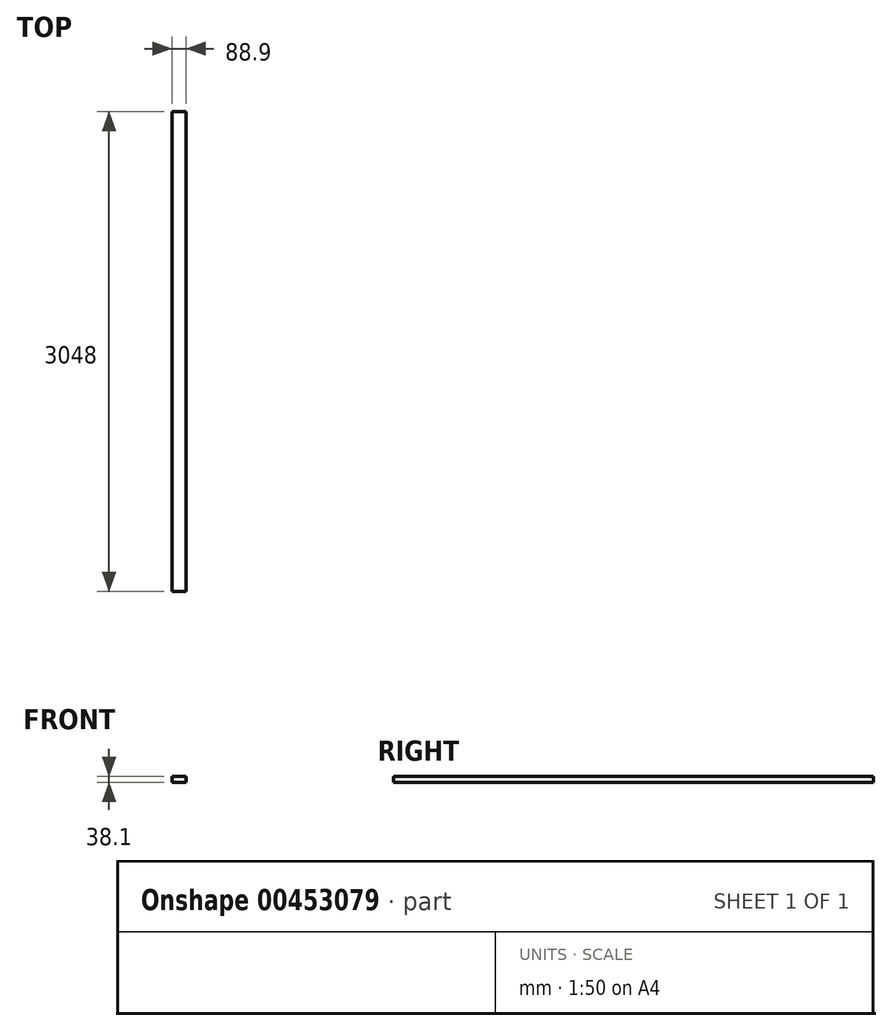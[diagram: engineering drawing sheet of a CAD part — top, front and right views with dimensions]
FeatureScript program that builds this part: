
annotation { "Feature Type Name" : "Feature", "Feature Type Description" : "" }
export const myFeature = defineFeature(function(context is Context, id is Id, definition is map)
    precondition{}
    {
        {
            var Q0;
            Q0=qCreatedBy(makeId("Front.planeOp"),FACE);
            var sketch = newSketch(context, id + "F0", { "sketchPlane" : qUnion([Q0])});
            skLineSegment(sketch, "E0.bottom", {"start": v(44.45, 19.05) * mm, "end": v(-44.45, 19.05) * mm});
            skLineSegment(sketch, "E0.top", {"start": v(44.45, -19.05) * mm, "end": v(-44.45, -19.05) * mm});
            skLineSegment(sketch, "E0.left", {"start": v(44.45, 19.05) * mm, "end": v(44.45, -19.05) * mm});
            skLineSegment(sketch, "E0.right", {"start": v(-44.45, 19.05) * mm, "end": v(-44.45, -19.05) * mm});
            skPoint(sketch, "E0.middle", {"position": v(0, 0) * mm});
            skSolve(sketch);
        }
        {
            var Q0;
            Q0 = qSketchRegion(id + "F0", true);
            extrude(context, id + "F1", {"entities" : qUnion([Q0]), "depth" : 3048 * mm, "offsetDistance" : 25.4 * mm});
        }
    });
